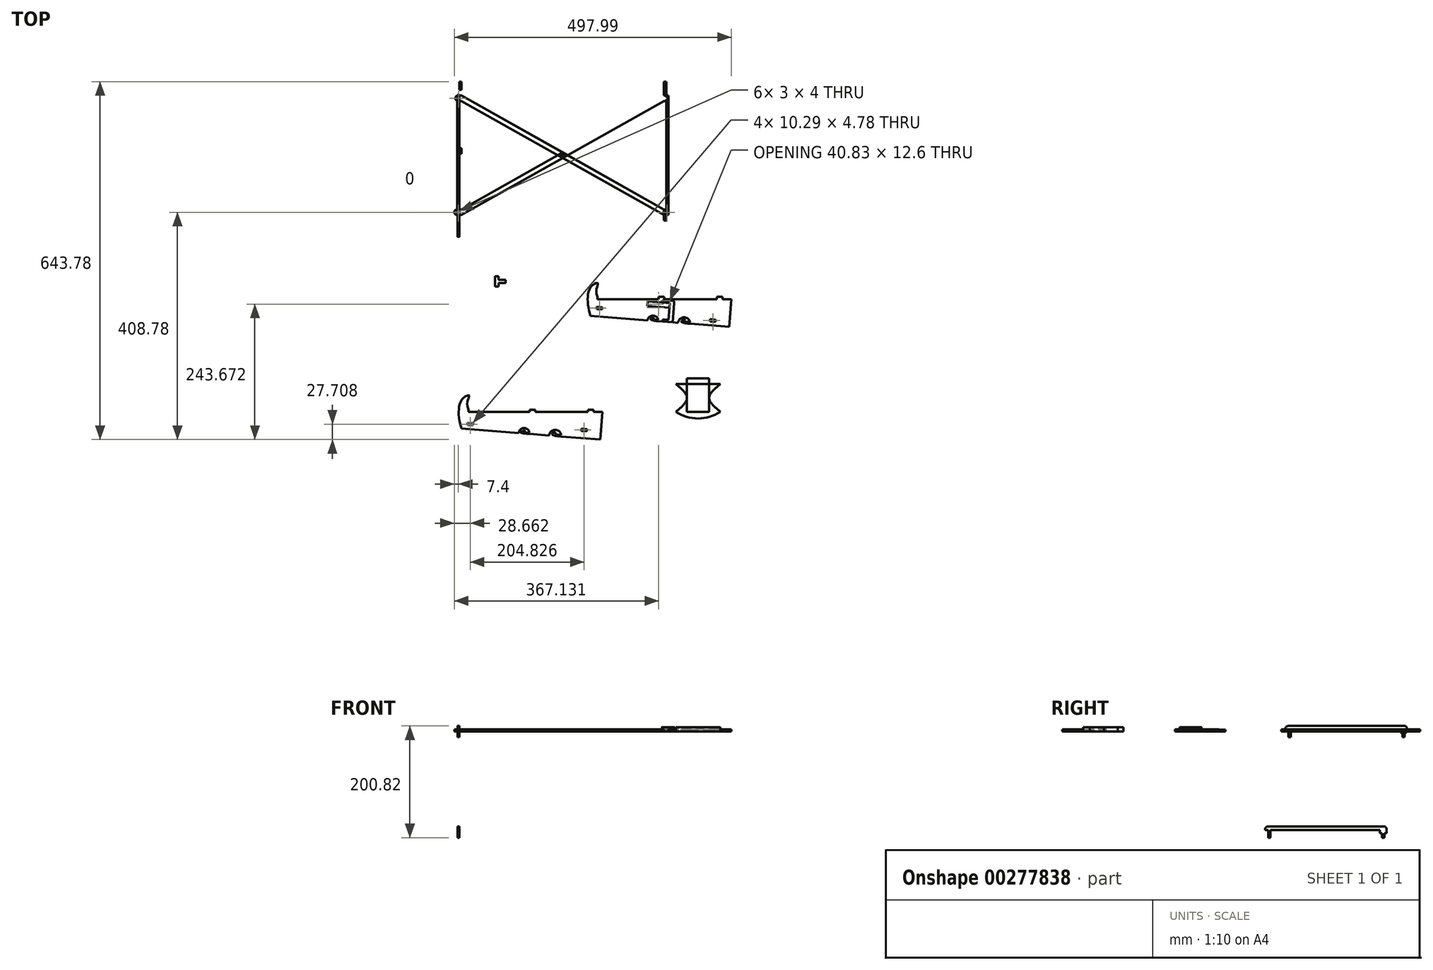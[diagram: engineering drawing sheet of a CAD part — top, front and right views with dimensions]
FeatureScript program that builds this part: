
annotation { "Feature Type Name" : "Feature", "Feature Type Description" : "" }
export const myFeature = defineFeature(function(context is Context, id is Id, definition is map)
    precondition{}
    {
        {
            var Q0;
            Q0=qCreatedBy(makeId("Top.planeOp"),FACE);
            var sketch = newSketch(context, id + "F0", { "sketchPlane" : qUnion([Q0])});
            skLineSegment(sketch, "E0.bottom", {"start": v(190, 125) * mm, "end": v(-190, 125) * mm});
            skLineSegment(sketch, "E0.top", {"start": v(190, -125) * mm, "end": v(-190, -125) * mm});
            skLineSegment(sketch, "E0.left", {"start": v(190, 125) * mm, "end": v(190, -125) * mm});
            skLineSegment(sketch, "E0.right", {"start": v(-190, 125) * mm, "end": v(-190, -125) * mm});
            skPoint(sketch, "E0.middle", {"position": v(0, 0) * mm});
            skLineSegment(sketch, "E1.right", {"start": v(-190, 125) * mm, "end": v(-190, -108) * mm});
            skLineSegment(sketch, "E2.bottom", {"start": v(-190, -125) * mm, "end": v(-186, -125) * mm});
            skLineSegment(sketch, "E2.top", {"start": v(-190, 125) * mm, "end": v(-186, 125) * mm});
            skLineSegment(sketch, "E2.left", {"start": v(-190, -125) * mm, "end": v(-190, -112) * mm});
            skLineSegment(sketch, "E2.right", {"start": v(-186, -125) * mm, "end": v(-186, -115) * mm});
            skLineSegment(sketch, "E3.bottom", {"start": v(190, -125) * mm, "end": v(186, -125) * mm});
            skLineSegment(sketch, "E3.top", {"start": v(190, 125) * mm, "end": v(186, 125) * mm});
            skLineSegment(sketch, "E3.left", {"start": v(190, -125) * mm, "end": v(190, 125) * mm});
            skLineSegment(sketch, "E3.right", {"start": v(186, -125) * mm, "end": v(186, 125) * mm});
            skLineSegment(sketch, "E4", {"start": v(49.8, -296.15) * mm, "end": v(152.32, -304.35) * mm});
            skLineSegment(sketch, "E5", {"start": v(299, -316.08) * mm, "end": v(303, -266.24) * mm});
            skLineSegment(sketch, "E6", {"start": v(303, -266.24) * mm, "end": v(287.2, -266.24) * mm});
            skLineSegment(sketch, "E7", {"start": v(52.2, -266.24) * mm, "end": v(49.8, -296.15) * mm, "construction": true});
            skLineSegment(sketch, "E8", {"start": v(0, 0) * mm, "end": v(0, 125) * mm, "construction": true});
            skLineSegment(sketch, "E9", {"start": v(0, 0) * mm, "end": v(0, -125) * mm, "construction": true});
            skLineSegment(sketch, "E10.bottom", {"start": v(-186, 125) * mm, "end": v(-182, 125) * mm});
            skLineSegment(sketch, "E10.top", {"start": v(-186, -125) * mm, "end": v(-182, -125) * mm});
            skLineSegment(sketch, "E10.left", {"start": v(-186, 125) * mm, "end": v(-186, 100) * mm});
            skLineSegment(sketch, "E10.right", {"start": v(-182, 125) * mm, "end": v(-182, 100) * mm});
            skLineSegment(sketch, "E11.MirrorCS", {"start": v(182, 125) * mm, "end": v(182, -125) * mm});
            skLineSegment(sketch, "E12", {"start": v(-186, -115) * mm, "end": v(-182, -115) * mm});
            skLineSegment(sketch, "E13", {"start": v(-186, 0) * mm, "end": v(186, 0) * mm, "construction": true});
            skLineSegment(sketch, "E14", {"start": v(-183.8, 0) * mm, "end": v(-183.8, 5) * mm, "construction": true});
            skLineSegment(sketch, "E15", {"start": v(-186, 5) * mm, "end": v(-182, 5) * mm});
            skLineSegment(sketch, "E16.MirrorCS", {"start": v(-186, -5) * mm, "end": v(-182, -5) * mm});
            skLineSegment(sketch, "E17", {"start": v(-186, 110) * mm, "end": v(-182, 110) * mm});
            skLineSegment(sketch, "E18", {"start": v(-186, 100) * mm, "end": v(-182, 100) * mm});
            skLineSegment(sketch, "E19", {"start": v(52.2, -266.24) * mm, "end": v(52.2, -242.24) * mm, "construction": true});
            skLineSegment(sketch, "E20", {"start": v(52.2, -242.24) * mm, "end": v(62.16, -243.04) * mm, "construction": true});
            skLineSegment(sketch, "E21", {"start": v(62.16, -243.04) * mm, "end": v(62.16, -266.24) * mm, "construction": true});
            skLineSegment(sketch, "E22.bottom", {"start": v(62.16, -266.24) * mm, "end": v(172.2, -266.24) * mm, "construction": true});
            skLineSegment(sketch, "E22.top", {"start": v(52.2, -262.24) * mm, "end": v(303, -262.24) * mm, "construction": true});
            skLineSegment(sketch, "E22.left", {"start": v(52.2, -266.24) * mm, "end": v(52.2, -262.24) * mm, "construction": true});
            skLineSegment(sketch, "E22.right", {"start": v(303, -266.24) * mm, "end": v(303, -262.24) * mm, "construction": true});
            skFitSpline(sketch, "E23", {"points": [v(49.8, -296.15) * mm, v(44.72, -265.8) * mm, v(52.2, -242.24) * mm, v(62.86, -237.24) * mm, v(62.38, -242.24) * mm, v(62.16, -262.24) * mm], "startDerivative": vector(-32.9, 108.57) * mm, "endDerivative": vector(52.9, -154.73) * mm});
            skLineSegment(sketch, "E24", {"start": v(62.16, -262.24) * mm, "end": v(62.16, -266.24) * mm});
            skLineSegment(sketch, "E25", {"start": v(302.2, -266.24) * mm, "end": v(302.2, -262.24) * mm, "construction": true});
            skLineSegment(sketch, "E26", {"start": v(287.2, -266.24) * mm, "end": v(287.2, -262.24) * mm});
            skLineSegment(sketch, "E27", {"start": v(287.2, -262.24) * mm, "end": v(277.2, -262.24) * mm});
            skLineSegment(sketch, "E28", {"start": v(277.2, -262.24) * mm, "end": v(277.2, -266.24) * mm});
            skLineSegment(sketch, "E29", {"start": v(182.2, -266.24) * mm, "end": v(182.2, -262.24) * mm});
            skLineSegment(sketch, "E30", {"start": v(172.2, -266.24) * mm, "end": v(172.2, -262.24) * mm});
            skLineSegment(sketch, "E31", {"start": v(172.2, -262.24) * mm, "end": v(182.2, -262.24) * mm});
            skLineSegment(sketch, "E32", {"start": v(-182, -105) * mm, "end": v(-186, -105) * mm});
            skLineSegment(sketch, "E33", {"start": v(-186, 90) * mm, "end": v(-182, 90) * mm});
            skLineSegment(sketch, "E34.MirrorCS", {"start": v(186, 125) * mm, "end": v(182, 125) * mm});
            skLineSegment(sketch, "E35.MirrorCS", {"start": v(186, -125) * mm, "end": v(182, -125) * mm});
            skLineSegment(sketch, "E36.MirrorCS", {"start": v(-190, -125) * mm, "end": v(190, -125) * mm});
            skLineSegment(sketch, "E37.MirrorCS", {"start": v(186, 110) * mm, "end": v(182, 110) * mm});
            skLineSegment(sketch, "E38.MirrorCS", {"start": v(183.8, 0) * mm, "end": v(183.8, 5) * mm, "construction": true});
            skLineSegment(sketch, "E39.MirrorCS", {"start": v(186, 100) * mm, "end": v(182, 100) * mm});
            skLineSegment(sketch, "E40.MirrorCS", {"start": v(182, -105) * mm, "end": v(186, -105) * mm});
            skLineSegment(sketch, "E41.MirrorCS", {"start": v(186, -5) * mm, "end": v(182, -5) * mm});
            skLineSegment(sketch, "E42.MirrorCS", {"start": v(186, 90) * mm, "end": v(182, 90) * mm});
            skLineSegment(sketch, "E43.MirrorCS", {"start": v(186, 5) * mm, "end": v(182, 5) * mm});
            skLineSegment(sketch, "E44.MirrorCS", {"start": v(186, -115) * mm, "end": v(182, -115) * mm});
            skLineSegment(sketch, "E45", {"start": v(-182, -115) * mm, "end": v(182, 90) * mm});
            skLineSegment(sketch, "E46", {"start": v(-182, -105) * mm, "end": v(182, 100) * mm});
            skLineSegment(sketch, "E47", {"start": v(-182, 90) * mm, "end": v(182, -115) * mm});
            skLineSegment(sketch, "E48", {"start": v(182, -105) * mm, "end": v(-182, 100) * mm});
            skLineSegment(sketch, "E49.trimOffspring", {"start": v(-186, -115) * mm, "end": v(-186, -125) * mm});
            skLineSegment(sketch, "E50.trimOffspring", {"start": v(-186, -105) * mm, "end": v(-186, 90) * mm});
            skLineSegment(sketch, "E51", {"start": v(-186, -105) * mm, "end": v(-190, -105) * mm});
            skLineSegment(sketch, "E52", {"start": v(-186, -115) * mm, "end": v(-190, -115) * mm});
            skArc(sketch, "E53", {"start": v(-190, -105) * mm, "mid": v(-195, -110) * mm, "end": v(-190, -115) * mm});
            skArc(sketch, "E54", {"start": v(-190, 99.76) * mm, "mid": v(-193.01, 94.84) * mm, "end": v(-190, 89.93) * mm});
            skLineSegment(sketch, "E55.trimOffspring", {"start": v(-186, 100) * mm, "end": v(-186, 125) * mm});
            skLineSegment(sketch, "E56.trimOffspring", {"start": v(-186, 90) * mm, "end": v(-186, -105) * mm});
            skLineSegment(sketch, "E57.trimOffspring", {"start": v(-182, 90) * mm, "end": v(-182, -125) * mm});
            skLineSegment(sketch, "E58.MirrorCS", {"start": v(186, -125) * mm, "end": v(186, -115) * mm});
            skLineSegment(sketch, "E59.MirrorCS", {"start": v(186, -115) * mm, "end": v(186, -125) * mm});
            skLineSegment(sketch, "E60.MirrorCS", {"start": v(186, -115) * mm, "end": v(190, -115) * mm});
            skLineSegment(sketch, "E61.MirrorCS", {"start": v(186, -105) * mm, "end": v(190, -105) * mm});
            skArc(sketch, "E62.MirrorCS", {"start": v(190, -105) * mm, "mid": v(195, -110) * mm, "end": v(190, -115) * mm});
            skLineSegment(sketch, "E63.MirrorCS", {"start": v(186, 100) * mm, "end": v(186, 125) * mm});
            skLineSegment(sketch, "E64.MirrorCS", {"start": v(182, 125) * mm, "end": v(182, 100) * mm});
            skLineSegment(sketch, "E65.MirrorCS", {"start": v(186, 125) * mm, "end": v(186, 100) * mm});
            skArc(sketch, "E66.MirrorCS", {"start": v(190, 99.76) * mm, "mid": v(193.01, 94.84) * mm, "end": v(190, 89.93) * mm});
            skLineSegment(sketch, "E67.MirrorCS", {"start": v(186, 90) * mm, "end": v(186, -105) * mm});
            skLineSegment(sketch, "E68.MirrorCS", {"start": v(186, -105) * mm, "end": v(186, 90) * mm});
            skLineSegment(sketch, "E69.MirrorCS", {"start": v(182, 90) * mm, "end": v(182, -125) * mm});
            skLineSegment(sketch, "E70", {"start": v(186, 100) * mm, "end": v(190, 99.76) * mm});
            skLineSegment(sketch, "E71", {"start": v(186, 90) * mm, "end": v(190, 89.93) * mm});
            skLineSegment(sketch, "E72", {"start": v(-186, 90) * mm, "end": v(-190, 89.93) * mm});
            skLineSegment(sketch, "E73", {"start": v(-186, 100) * mm, "end": v(-190, 99.76) * mm});
            skLineSegment(sketch, "E74.trimOffspring", {"start": v(182.2, -266.24) * mm, "end": v(277.2, -266.24) * mm, "construction": true});
            skLineSegment(sketch, "E75.trimOffspring", {"start": v(172.2, -266.24) * mm, "end": v(62.16, -266.24) * mm});
            skLineSegment(sketch, "E76.trimOffspring", {"start": v(287.2, -266.24) * mm, "end": v(303, -266.24) * mm, "construction": true});
            skLineSegment(sketch, "E77.trimOffspring", {"start": v(277.2, -266.24) * mm, "end": v(182.2, -266.24) * mm});
            skLineSegment(sketch, "E78", {"start": v(50.88, -283.2) * mm, "end": v(300.08, -303.13) * mm, "construction": true});
            skLineSegment(sketch, "E79", {"start": v(51.2, -279.2) * mm, "end": v(197.94, -290.94) * mm, "construction": true});
            skLineSegment(sketch, "E80", {"start": v(275.12, -301.13) * mm, "end": v(275.44, -297.14) * mm});
            skLineSegment(sketch, "E81", {"start": v(275.44, -297.14) * mm, "end": v(265.47, -296.35) * mm});
            skLineSegment(sketch, "E82", {"start": v(265.47, -296.35) * mm, "end": v(265.15, -300.33) * mm});
            skLineSegment(sketch, "E83", {"start": v(265.15, -300.33) * mm, "end": v(275.12, -301.13) * mm});
            skLineSegment(sketch, "E84", {"start": v(60.8, -283.99) * mm, "end": v(61.13, -280) * mm});
            skLineSegment(sketch, "E85", {"start": v(71.1, -280.8) * mm, "end": v(70.77, -284.78) * mm});
            skLineSegment(sketch, "E86", {"start": v(61.13, -280) * mm, "end": v(71.1, -280.8) * mm});
            skLineSegment(sketch, "E87", {"start": v(70.77, -284.78) * mm, "end": v(60.8, -283.99) * mm});
            skLineSegment(sketch, "E88", {"start": v(265.47, -296.35) * mm, "end": v(264.12, -313.3) * mm, "construction": true});
            skLineSegment(sketch, "E89", {"start": v(275.44, -297.14) * mm, "end": v(274.09, -314.1) * mm, "construction": true});
            skLineSegment(sketch, "E90", {"start": v(264.68, -306.32) * mm, "end": v(274.64, -307.11) * mm});
            skLineSegment(sketch, "E91", {"start": v(265, -302.33) * mm, "end": v(274.96, -303.13) * mm});
            skLineSegment(sketch, "E92", {"start": v(265, -302.33) * mm, "end": v(264.68, -306.32) * mm});
            skLineSegment(sketch, "E93", {"start": v(274.96, -303.13) * mm, "end": v(274.64, -307.11) * mm});
            skLineSegment(sketch, "E94", {"start": v(61.13, -280) * mm, "end": v(59.77, -296.95) * mm, "construction": true});
            skLineSegment(sketch, "E95", {"start": v(60.65, -285.98) * mm, "end": v(70.62, -286.78) * mm});
            skLineSegment(sketch, "E96", {"start": v(60.33, -289.97) * mm, "end": v(70.3, -290.77) * mm});
            skLineSegment(sketch, "E97", {"start": v(70.3, -290.77) * mm, "end": v(70.62, -286.78) * mm});
            skLineSegment(sketch, "E98", {"start": v(60.65, -285.98) * mm, "end": v(60.33, -289.97) * mm});
            skLineSegment(sketch, "E99", {"start": v(-182, -498.85) * mm, "end": v(-79.55, -507.04) * mm});
            skLineSegment(sketch, "E100", {"start": v(67.2, -518.78) * mm, "end": v(71.18, -468.94) * mm});
            skLineSegment(sketch, "E101", {"start": v(71.18, -468.94) * mm, "end": v(55.38, -468.94) * mm});
            skLineSegment(sketch, "E102", {"start": v(-179.62, -468.94) * mm, "end": v(-182, -498.85) * mm, "construction": true});
            skLineSegment(sketch, "E103", {"start": v(-179.62, -468.94) * mm, "end": v(-179.62, -444.94) * mm, "construction": true});
            skLineSegment(sketch, "E104", {"start": v(-179.62, -444.94) * mm, "end": v(-169.65, -445.74) * mm, "construction": true});
            skLineSegment(sketch, "E105", {"start": v(-169.65, -445.74) * mm, "end": v(-169.65, -468.94) * mm, "construction": true});
            skLineSegment(sketch, "E106.bottom", {"start": v(-169.65, -468.94) * mm, "end": v(-59.62, -468.94) * mm, "construction": true});
            skLineSegment(sketch, "E106.top", {"start": v(-179.62, -464.94) * mm, "end": v(71.18, -464.94) * mm, "construction": true});
            skLineSegment(sketch, "E106.left", {"start": v(-179.62, -468.94) * mm, "end": v(-179.62, -464.94) * mm, "construction": true});
            skLineSegment(sketch, "E106.right", {"start": v(71.18, -468.94) * mm, "end": v(71.18, -464.94) * mm, "construction": true});
            skFitSpline(sketch, "E107", {"points": [v(-182, -498.85) * mm, v(-187.09, -467.99) * mm, v(-179.62, -444.94) * mm, v(-168.95, -439.42) * mm, v(-169.43, -444.94) * mm, v(-169.65, -464.94) * mm], "startDerivative": vector(-32.9, 108.57) * mm, "endDerivative": vector(52.9, -154.73) * mm});
            skLineSegment(sketch, "E108", {"start": v(-169.65, -464.94) * mm, "end": v(-169.65, -468.94) * mm});
            skLineSegment(sketch, "E109", {"start": v(70.38, -468.94) * mm, "end": v(70.38, -464.94) * mm, "construction": true});
            skLineSegment(sketch, "E110", {"start": v(55.38, -468.94) * mm, "end": v(55.38, -464.94) * mm});
            skLineSegment(sketch, "E111", {"start": v(55.38, -464.94) * mm, "end": v(45.38, -464.94) * mm});
            skLineSegment(sketch, "E112", {"start": v(45.38, -464.94) * mm, "end": v(45.38, -468.94) * mm});
            skLineSegment(sketch, "E113", {"start": v(-49.62, -468.94) * mm, "end": v(-49.62, -464.94) * mm});
            skLineSegment(sketch, "E114", {"start": v(-59.62, -468.94) * mm, "end": v(-59.62, -464.94) * mm});
            skLineSegment(sketch, "E115", {"start": v(-59.62, -464.94) * mm, "end": v(-49.62, -464.94) * mm});
            skLineSegment(sketch, "E116.trimOffspring", {"start": v(-49.62, -468.94) * mm, "end": v(45.38, -468.94) * mm, "construction": true});
            skLineSegment(sketch, "E117.trimOffspring", {"start": v(-59.62, -468.94) * mm, "end": v(-169.65, -468.94) * mm});
            skLineSegment(sketch, "E118.trimOffspring", {"start": v(55.38, -468.94) * mm, "end": v(71.18, -468.94) * mm, "construction": true});
            skLineSegment(sketch, "E119.trimOffspring", {"start": v(45.38, -468.94) * mm, "end": v(-49.62, -468.94) * mm});
            skLineSegment(sketch, "E120", {"start": v(-180.97, -485.89) * mm, "end": v(68.23, -505.82) * mm, "construction": true});
            skLineSegment(sketch, "E121", {"start": v(-180.65, -481.9) * mm, "end": v(68.55, -501.84) * mm, "construction": true});
            skLineSegment(sketch, "E122", {"start": v(43.31, -503.83) * mm, "end": v(43.63, -499.84) * mm});
            skLineSegment(sketch, "E123", {"start": v(43.63, -499.84) * mm, "end": v(33.66, -499.05) * mm});
            skLineSegment(sketch, "E124", {"start": v(33.66, -499.05) * mm, "end": v(33.34, -503.03) * mm});
            skLineSegment(sketch, "E125", {"start": v(33.34, -503.03) * mm, "end": v(43.31, -503.83) * mm});
            skLineSegment(sketch, "E126", {"start": v(-171, -486.69) * mm, "end": v(-170.68, -482.7) * mm});
            skLineSegment(sketch, "E127", {"start": v(-160.72, -483.5) * mm, "end": v(-161.03, -487.48) * mm});
            skLineSegment(sketch, "E128", {"start": v(-170.68, -482.7) * mm, "end": v(-160.72, -483.5) * mm});
            skLineSegment(sketch, "E129", {"start": v(-161.03, -487.48) * mm, "end": v(-171, -486.69) * mm});
            skLineSegment(sketch, "E130", {"start": v(33.66, -499.05) * mm, "end": v(32.3, -516) * mm, "construction": true});
            skLineSegment(sketch, "E131", {"start": v(43.63, -499.84) * mm, "end": v(42.28, -516.79) * mm, "construction": true});
            skLineSegment(sketch, "E132", {"start": v(32.87, -509.01) * mm, "end": v(42.83, -509.81) * mm});
            skLineSegment(sketch, "E133", {"start": v(33.19, -505.03) * mm, "end": v(43.15, -505.82) * mm});
            skLineSegment(sketch, "E134", {"start": v(33.19, -505.03) * mm, "end": v(32.87, -509.01) * mm});
            skLineSegment(sketch, "E135", {"start": v(43.15, -505.82) * mm, "end": v(42.83, -509.81) * mm});
            skLineSegment(sketch, "E136", {"start": v(-170.68, -482.7) * mm, "end": v(-172.04, -499.64) * mm, "construction": true});
            skLineSegment(sketch, "E137", {"start": v(-171.16, -488.68) * mm, "end": v(-161.2, -489.48) * mm});
            skLineSegment(sketch, "E138", {"start": v(-171.48, -492.67) * mm, "end": v(-161.51, -493.46) * mm});
            skLineSegment(sketch, "E139", {"start": v(-161.51, -493.46) * mm, "end": v(-161.2, -489.48) * mm});
            skLineSegment(sketch, "E140", {"start": v(-171.16, -488.68) * mm, "end": v(-171.48, -492.67) * mm});
            skLineSegment(sketch, "E141.MirrorCS", {"start": v(-190, -125) * mm, "end": v(-190, 125) * mm});
            skLineSegment(sketch, "E142.trimOffspring", {"start": v(-190, -108) * mm, "end": v(-190, 125) * mm});
            skLineSegment(sketch, "E143.trimOffspring", {"start": v(-190, -110) * mm, "end": v(-190, -125) * mm});
            skLineSegment(sketch, "E144.bottom", {"start": v(-189, 96.84) * mm, "end": v(-186, 96.84) * mm, "construction": true});
            skLineSegment(sketch, "E144.top", {"start": v(-189, 92.84) * mm, "end": v(-186, 92.84) * mm, "construction": true});
            skLineSegment(sketch, "E144.left", {"start": v(-189, 96.84) * mm, "end": v(-189, 92.84) * mm, "construction": true});
            skLineSegment(sketch, "E144.right", {"start": v(-186, 96.84) * mm, "end": v(-186, 92.84) * mm, "construction": true});
            skLineSegment(sketch, "E145.MirrorCS", {"start": v(189, 92.84) * mm, "end": v(186, 92.84) * mm});
            skLineSegment(sketch, "E146.MirrorCS", {"start": v(189, 96.84) * mm, "end": v(186, 96.84) * mm});
            skLineSegment(sketch, "E147.MirrorCS", {"start": v(189, 96.84) * mm, "end": v(189, 92.84) * mm});
            skLineSegment(sketch, "E148.MirrorCS", {"start": v(186, 96.84) * mm, "end": v(186, 92.84) * mm});
            skLineSegment(sketch, "E149.bottom", {"start": v(-186.1, -112) * mm, "end": v(-189.1, -112) * mm});
            skLineSegment(sketch, "E149.top", {"start": v(-186.1, -108) * mm, "end": v(-189.1, -108) * mm});
            skLineSegment(sketch, "E149.left", {"start": v(-186.1, -112) * mm, "end": v(-186.1, -108) * mm});
            skLineSegment(sketch, "E149.right", {"start": v(-189.1, -112) * mm, "end": v(-189.1, -108) * mm});
            skLineSegment(sketch, "E150", {"start": v(-186, -105) * mm, "end": v(-186, -115) * mm, "construction": true});
            skLineSegment(sketch, "E151.MirrorCS", {"start": v(190, -108) * mm, "end": v(190, 125) * mm});
            skLineSegment(sketch, "E152.MirrorCS", {"start": v(190, -110) * mm, "end": v(190, -125) * mm});
            skLineSegment(sketch, "E153.MirrorCS", {"start": v(186, -105) * mm, "end": v(186, -115) * mm, "construction": true});
            skLineSegment(sketch, "E154.MirrorCS", {"start": v(190, 125) * mm, "end": v(190, -108) * mm});
            skLineSegment(sketch, "E155.MirrorCS", {"start": v(186.1, -112) * mm, "end": v(189.1, -112) * mm});
            skLineSegment(sketch, "E156.MirrorCS", {"start": v(190, -125) * mm, "end": v(190, -112) * mm});
            skLineSegment(sketch, "E157.MirrorCS", {"start": v(186.1, -112) * mm, "end": v(186.1, -108) * mm});
            skLineSegment(sketch, "E158.MirrorCS", {"start": v(189.1, -112) * mm, "end": v(189.1, -108) * mm});
            skLineSegment(sketch, "E159.MirrorCS", {"start": v(186.1, -108) * mm, "end": v(189.1, -108) * mm});
            skLineSegment(sketch, "E160", {"start": v(-186, 90) * mm, "end": v(-186, 100) * mm, "construction": true});
            skLineSegment(sketch, "E161.bottom", {"start": v(-189, 96.84) * mm, "end": v(-186, 96.84) * mm});
            skLineSegment(sketch, "E161.top", {"start": v(-189, 92.84) * mm, "end": v(-186, 92.84) * mm});
            skLineSegment(sketch, "E161.left", {"start": v(-189, 96.84) * mm, "end": v(-189, 92.84) * mm});
            skLineSegment(sketch, "E161.right", {"start": v(-186, 96.84) * mm, "end": v(-186, 92.84) * mm});
            skLineSegment(sketch, "E162", {"start": v(8.88, -7.5) * mm, "end": v(-8.88, -7.5) * mm, "construction": true});
            skLineSegment(sketch, "E163.bottom", {"start": v(3, -9) * mm, "end": v(-3, -9) * mm});
            skLineSegment(sketch, "E163.top", {"start": v(3, -6) * mm, "end": v(-3, -6) * mm});
            skLineSegment(sketch, "E163.left", {"start": v(3, -9) * mm, "end": v(3, -6) * mm});
            skLineSegment(sketch, "E163.right", {"start": v(-3, -9) * mm, "end": v(-3, -6) * mm});
            skPoint(sketch, "E163.middle", {"position": v(0, -7.5) * mm});
            skLineSegment(sketch, "E164.bottom", {"start": v(-115.58, -237.46) * mm, "end": v(-102.58, -237.46) * mm});
            skLineSegment(sketch, "E164.top", {"start": v(-115.58, -231.46) * mm, "end": v(-102.58, -231.46) * mm});
            skLineSegment(sketch, "E164.left", {"start": v(-121.58, -237.46) * mm, "end": v(-121.58, -231.46) * mm});
            skLineSegment(sketch, "E164.right", {"start": v(-102.58, -237.46) * mm, "end": v(-102.58, -231.46) * mm});
            skPoint(sketch, "E164.middle", {"position": v(-112.08, -234.46) * mm});
            skLineSegment(sketch, "E165.top", {"start": v(-121.58, -243.46) * mm, "end": v(-115.58, -243.46) * mm});
            skLineSegment(sketch, "E165.left", {"start": v(-121.58, -231.46) * mm, "end": v(-121.58, -243.46) * mm});
            skLineSegment(sketch, "E165.right", {"start": v(-115.58, -231.46) * mm, "end": v(-115.58, -243.46) * mm});
            skLineSegment(sketch, "E166", {"start": v(-105.58, -231.46) * mm, "end": v(-105.58, -237.46) * mm, "construction": true});
            skLineSegment(sketch, "E167", {"start": v(-121.58, -231.46) * mm, "end": v(-121.58, -225.46) * mm});
            skLineSegment(sketch, "E168", {"start": v(-121.58, -225.46) * mm, "end": v(-115.58, -225.46) * mm});
            skLineSegment(sketch, "E169", {"start": v(-115.58, -225.46) * mm, "end": v(-115.58, -231.46) * mm});
            skLineSegment(sketch, "E170", {"start": v(191.59, -281.4) * mm, "end": v(151.72, -278.22) * mm});
            skLineSegment(sketch, "E171", {"start": v(151.72, -278.22) * mm, "end": v(152.35, -270.24) * mm});
            skLineSegment(sketch, "E172", {"start": v(152.35, -270.24) * mm, "end": v(192.23, -273.43) * mm});
            skLineSegment(sketch, "E173", {"start": v(192.23, -273.43) * mm, "end": v(191.59, -281.4) * mm});
            skLineSegment(sketch, "E174.trimOffspring", {"start": v(237.81, -294.13) * mm, "end": v(300.4, -299.14) * mm, "construction": true});
            skLineSegment(sketch, "E175", {"start": v(200.25, -273.43) * mm, "end": v(197.49, -307.96) * mm});
            skLineSegment(sketch, "E176", {"start": v(179.56, -306.53) * mm, "end": v(179.88, -302.54) * mm});
            skLineSegment(sketch, "E177", {"start": v(179.88, -302.54) * mm, "end": v(189.85, -303.34) * mm});
            skLineSegment(sketch, "E178", {"start": v(179.56, -306.53) * mm, "end": v(197.49, -307.96) * mm});
            skLineSegment(sketch, "E179", {"start": v(191.59, -281.4) * mm, "end": v(189.52, -307.32) * mm});
            skLineSegment(sketch, "E180", {"start": v(181.86, -302.7) * mm, "end": v(181.54, -306.69) * mm});
            skLineSegment(sketch, "E181.bottom", {"start": v(223.2, -408.84) * mm, "end": v(263.2, -408.84) * mm});
            skLineSegment(sketch, "E181.top", {"start": v(223.2, -418.84) * mm, "end": v(263.2, -418.84) * mm});
            skLineSegment(sketch, "E181.left", {"start": v(223.2, -408.84) * mm, "end": v(223.2, -418.84) * mm});
            skLineSegment(sketch, "E181.right", {"start": v(263.2, -408.84) * mm, "end": v(263.2, -418.84) * mm});
            skLineSegment(sketch, "E182.bottom", {"start": v(223.2, -418.84) * mm, "end": v(271.68, -418.84) * mm});
            skLineSegment(sketch, "E182.top", {"start": v(223.2, -468.84) * mm, "end": v(263.2, -468.84) * mm});
            skLineSegment(sketch, "E182.left", {"start": v(223.2, -418.84) * mm, "end": v(223.2, -468.84) * mm});
            skLineSegment(sketch, "E183", {"start": v(263.2, -418.84) * mm, "end": v(283.2, -418.84) * mm});
            skLineSegment(sketch, "E184", {"start": v(223.2, -418.84) * mm, "end": v(203.2, -418.84) * mm});
            skLineSegment(sketch, "E185", {"start": v(263.2, -418.84) * mm, "end": v(263.2, -468.84) * mm});
            skLineSegment(sketch, "E186", {"start": v(203.2, -468.84) * mm, "end": v(223.2, -468.84) * mm});
            skFitSpline(sketch, "E187", {"points": [v(203.2, -418.84) * mm, v(223.2, -443.84) * mm, v(203.2, -468.84) * mm], "startDerivative": vector(60, -50) * mm, "endDerivative": vector(-60, -50) * mm});
            skLineSegment(sketch, "E188", {"start": v(243.2, -408.84) * mm, "end": v(243.2, -468.84) * mm, "construction": true});
            skFitSpline(sketch, "E189.MirrorCS", {"points": [v(283.2, -418.84) * mm, v(263.2, -443.84) * mm, v(283.2, -468.84) * mm], "startDerivative": vector(-60, -50) * mm, "endDerivative": vector(60, -50) * mm});
            skLineSegment(sketch, "E190.MirrorCS", {"start": v(283.2, -468.84) * mm, "end": v(263.2, -468.84) * mm});
            skArc(sketch, "E191", {"start": v(203.2, -468.84) * mm, "mid": v(243.2, -480.84) * mm, "end": v(283.2, -468.84) * mm});
            skLineSegment(sketch, "E192", {"start": v(186.56, -268.97) * mm, "end": v(182.58, -268.65) * mm});
            skLineSegment(sketch, "E193", {"start": v(182.58, -268.65) * mm, "end": v(182.26, -272.64) * mm});
            skLineSegment(sketch, "E194", {"start": v(192.23, -273.43) * mm, "end": v(192.55, -269.45) * mm});
            skLineSegment(sketch, "E195", {"start": v(192.55, -269.45) * mm, "end": v(186.56, -268.97) * mm});
            skLineSegment(sketch, "E196", {"start": v(184.57, -268.8) * mm, "end": v(184.25, -272.8) * mm});
            skFitSpline(sketch, "E197", {"points": [v(192.55, -269.45) * mm, v(199.31, -269.66) * mm, v(200.25, -273.43) * mm], "startDerivative": vector(15.87, 5.36) * mm, "endDerivative": vector(-1.15, -11.12) * mm});
            skLineSegment(sketch, "E198", {"start": v(182.58, -268.65) * mm, "end": v(180.58, -268.49) * mm});
            skFitSpline(sketch, "E199", {"points": [v(180.58, -268.49) * mm, v(178.6, -272.34) * mm], "startDerivative": vector(-6.52, -3.18) * mm, "endDerivative": vector(0.58, -3.67) * mm});
            skLineSegment(sketch, "E200", {"start": v(172.2, -266.24) * mm, "end": v(172.2, -305.94) * mm, "construction": true});
            skArc(sketch, "E201", {"start": v(171.92, -303.6) * mm, "mid": v(161.81, -295.95) * mm, "end": v(152.32, -304.35) * mm});
            skLineSegment(sketch, "E202", {"start": v(-59.62, -468.94) * mm, "end": v(-59.62, -507.28) * mm, "construction": true});
            skArc(sketch, "E203", {"start": v(-2.9, -510.02) * mm, "mid": v(-14.37, -501.34) * mm, "end": v(-24.62, -511.44) * mm});
            skLineSegment(sketch, "E204.trimOffspring", {"start": v(-59.62, -508.64) * mm, "end": v(-24.62, -511.44) * mm});
            skLineSegment(sketch, "E205.trimOffspring", {"start": v(-2.69, -513.2) * mm, "end": v(67.2, -518.78) * mm});
            skFitSpline(sketch, "E206", {"points": [v(-2.69, -513.2) * mm, v(-15.78, -511.43) * mm, v(-19.23, -509.19) * mm, v(-17.76, -506.59) * mm, v(-13.38, -506.25) * mm, v(-14.8, -508.21) * mm, v(-2.69, -511.44) * mm], "startDerivative": vector(-44.09, 4) * mm, "endDerivative": vector(41.48, -21.36) * mm});
            skFitSpline(sketch, "E207", {"points": [v(-59.62, -508.64) * mm, v(-75.41, -506.11) * mm, v(-74.67, -504.74) * mm, v(-71.74, -503.03) * mm, v(-68.32, -502.54) * mm, v(-68.95, -504.77) * mm, v(-59.72, -506.6) * mm], "startDerivative": vector(-44.09, 4) * mm, "endDerivative": vector(48.5, -6.14) * mm});
            skArc(sketch, "E208.trimOffspring", {"start": v(-59.72, -506.6) * mm, "mid": v(-69.83, -498.12) * mm, "end": v(-79.55, -507.04) * mm});
            skFitSpline(sketch, "E209", {"points": [v(172.13, -305.97) * mm, v(161.88, -304.33) * mm, v(157.84, -302.36) * mm, v(159.8, -299.35) * mm, v(163.27, -298.58) * mm, v(162.56, -301.53) * mm, v(172.2, -303.64) * mm], "startDerivative": vector(-44.09, 4) * mm, "endDerivative": vector(48.5, -6.14) * mm});
            skLineSegment(sketch, "E210.trimOffspring", {"start": v(170.42, -305.8) * mm, "end": v(207.13, -308.73) * mm});
            skArc(sketch, "E211", {"start": v(228.8, -307.7) * mm, "mid": v(217.53, -299.03) * mm, "end": v(207.13, -308.73) * mm});
            skFitSpline(sketch, "E212", {"points": [v(229.05, -310.49) * mm, v(216.5, -308.58) * mm, v(212.99, -306.61) * mm, v(215.8, -303.95) * mm, v(219.36, -302.92) * mm, v(218.14, -305.54) * mm, v(229.73, -307.84) * mm], "startDerivative": vector(-44.09, 4) * mm, "endDerivative": vector(48.04, -9.09) * mm});
            skLineSegment(sketch, "E213.trimOffspring", {"start": v(229.05, -310.49) * mm, "end": v(299, -316.08) * mm});
            skLineSegment(sketch, "E214", {"start": v(-8.02, -510.02) * mm, "end": v(-2.9, -510.02) * mm});
            skLineSegment(sketch, "E215", {"start": v(-170.68, -482.7) * mm, "end": v(-169.97, -473.73) * mm, "construction": true});
            skLineSegment(sketch, "E216", {"start": v(-169.97, -473.73) * mm, "end": v(44.35, -490.87) * mm, "construction": true});
            skLineSegment(sketch, "E217", {"start": v(44.35, -490.87) * mm, "end": v(43.63, -499.84) * mm, "construction": true});
            skLineSegment(sketch, "E218", {"start": v(-169.97, -473.73) * mm, "end": v(-169.65, -468.94) * mm, "construction": true});
            skLineSegment(sketch, "E219", {"start": v(458.34, 154.63) * mm, "end": v(462.34, 154.63) * mm});
            skLineSegment(sketch, "E220", {"start": v(458.34, 144.63) * mm, "end": v(462.34, 144.63) * mm});
            skLineSegment(sketch, "E221", {"start": v(462.34, 144.63) * mm, "end": v(826.34, -60.37) * mm});
            skLineSegment(sketch, "E222", {"start": v(826.34, -50.37) * mm, "end": v(462.34, 154.63) * mm});
            skArc(sketch, "E223", {"start": v(454.34, 154.39) * mm, "mid": v(451.32, 149.47) * mm, "end": v(454.34, 144.56) * mm});
            skLineSegment(sketch, "E224.MirrorCS", {"start": v(830.34, -60.37) * mm, "end": v(834.34, -60.37) * mm});
            skLineSegment(sketch, "E225.MirrorCS", {"start": v(830.34, -60.37) * mm, "end": v(826.34, -60.37) * mm});
            skLineSegment(sketch, "E226.MirrorCS", {"start": v(826.34, -50.37) * mm, "end": v(830.34, -50.37) * mm});
            skLineSegment(sketch, "E227.MirrorCS", {"start": v(830.34, -50.37) * mm, "end": v(834.34, -50.37) * mm});
            skArc(sketch, "E228.MirrorCS", {"start": v(834.34, -50.37) * mm, "mid": v(839.34, -55.37) * mm, "end": v(834.34, -60.37) * mm});
            skLineSegment(sketch, "E229", {"start": v(458.34, 144.63) * mm, "end": v(454.34, 144.56) * mm});
            skLineSegment(sketch, "E230", {"start": v(458.34, 154.63) * mm, "end": v(454.34, 154.39) * mm});
            skLineSegment(sketch, "E231.bottom", {"start": v(455.34, 151.47) * mm, "end": v(458.34, 151.47) * mm, "construction": true});
            skLineSegment(sketch, "E231.top", {"start": v(455.34, 147.47) * mm, "end": v(458.34, 147.47) * mm, "construction": true});
            skLineSegment(sketch, "E231.left", {"start": v(455.34, 151.47) * mm, "end": v(455.34, 147.47) * mm, "construction": true});
            skLineSegment(sketch, "E232.MirrorCS", {"start": v(830.44, -57.37) * mm, "end": v(833.44, -57.37) * mm});
            skLineSegment(sketch, "E233.MirrorCS", {"start": v(830.44, -57.37) * mm, "end": v(830.44, -53.37) * mm});
            skLineSegment(sketch, "E234.MirrorCS", {"start": v(833.44, -57.37) * mm, "end": v(833.44, -53.37) * mm});
            skLineSegment(sketch, "E235.MirrorCS", {"start": v(830.44, -53.37) * mm, "end": v(833.44, -53.37) * mm});
            skLineSegment(sketch, "E236", {"start": v(458.34, 144.63) * mm, "end": v(458.34, 154.63) * mm, "construction": true});
            skLineSegment(sketch, "E237.bottom", {"start": v(647.34, 45.63) * mm, "end": v(641.34, 45.63) * mm});
            skLineSegment(sketch, "E237.top", {"start": v(647.34, 48.63) * mm, "end": v(641.34, 48.63) * mm});
            skLineSegment(sketch, "E237.left", {"start": v(647.34, 45.63) * mm, "end": v(647.34, 48.63) * mm});
            skLineSegment(sketch, "E237.right", {"start": v(641.34, 45.63) * mm, "end": v(641.34, 48.63) * mm});
            skLineSegment(sketch, "E238.bottom", {"start": v(455.34, 151.47) * mm, "end": v(458.34, 151.47) * mm});
            skLineSegment(sketch, "E238.top", {"start": v(455.34, 147.47) * mm, "end": v(458.34, 147.47) * mm});
            skLineSegment(sketch, "E238.left", {"start": v(455.34, 151.47) * mm, "end": v(455.34, 147.47) * mm});
            skLineSegment(sketch, "E238.right", {"start": v(458.34, 151.47) * mm, "end": v(458.34, 147.47) * mm});
            skLineSegment(sketch, "E239", {"start": v(462.1, 74.96) * mm, "end": v(464.4, 71.68) * mm});
            skLineSegment(sketch, "E240", {"start": v(472.58, 77.41) * mm, "end": v(470.29, 80.7) * mm});
            skLineSegment(sketch, "E241", {"start": v(464.4, 71.68) * mm, "end": v(841.1, -108.9) * mm});
            skLineSegment(sketch, "E242", {"start": v(472.58, 77.41) * mm, "end": v(849.3, -103.17) * mm});
            skLineSegment(sketch, "E243", {"start": v(470.29, 80.7) * mm, "end": v(468, 83.97) * mm});
            skLineSegment(sketch, "E244", {"start": v(462.1, 74.96) * mm, "end": v(459.8, 78.23) * mm});
            skArc(sketch, "E245", {"start": v(468, 83.97) * mm, "mid": v(461.03, 85.2) * mm, "end": v(459.8, 78.23) * mm});
            skLineSegment(sketch, "E246.MirrorCS", {"start": v(851.59, -106.45) * mm, "end": v(849.3, -103.17) * mm});
            skLineSegment(sketch, "E247.MirrorCS", {"start": v(843.4, -112.19) * mm, "end": v(841.1, -108.9) * mm});
            skArc(sketch, "E248.MirrorCS", {"start": v(853.68, -109.87) * mm, "mid": v(851.38, -115.15) * mm, "end": v(845.63, -115.5) * mm});
            skLineSegment(sketch, "E249", {"start": v(851.59, -106.45) * mm, "end": v(853.68, -109.87) * mm});
            skLineSegment(sketch, "E250", {"start": v(843.4, -112.19) * mm, "end": v(845.63, -115.5) * mm});
            skLineSegment(sketch, "E251.MirrorCS", {"start": v(847.44, -113.01) * mm, "end": v(845.72, -110.56) * mm});
            skLineSegment(sketch, "E252.MirrorCS", {"start": v(850.72, -110.72) * mm, "end": v(849, -108.26) * mm});
            skLineSegment(sketch, "E253.MirrorCS", {"start": v(850.72, -110.72) * mm, "end": v(847.44, -113.01) * mm});
            skLineSegment(sketch, "E254.bottom", {"start": v(464.5, 76.76) * mm, "end": v(462.78, 79.22) * mm});
            skLineSegment(sketch, "E254.top", {"start": v(467.77, 79.05) * mm, "end": v(466.05, 81.5) * mm});
            skLineSegment(sketch, "E254.left", {"start": v(464.5, 76.76) * mm, "end": v(467.77, 79.05) * mm});
            skLineSegment(sketch, "E254.right", {"start": v(462.78, 79.22) * mm, "end": v(466.05, 81.5) * mm});
            skLineSegment(sketch, "E255.bottom", {"start": v(657.33, -19.07) * mm, "end": v(653.9, -14.15) * mm});
            skLineSegment(sketch, "E255.top", {"start": v(659.8, -17.34) * mm, "end": v(656.35, -12.43) * mm});
            skLineSegment(sketch, "E255.left", {"start": v(657.33, -19.07) * mm, "end": v(659.8, -17.34) * mm});
            skLineSegment(sketch, "E255.right", {"start": v(653.9, -14.15) * mm, "end": v(656.35, -12.43) * mm});
            skLineSegment(sketch, "E256.bottom", {"start": v(1328.61, 202.88) * mm, "end": v(948.61, 202.88) * mm});
            skLineSegment(sketch, "E256.top", {"start": v(1328.61, -47.12) * mm, "end": v(948.61, -47.12) * mm});
            skLineSegment(sketch, "E256.left", {"start": v(1328.61, 202.88) * mm, "end": v(1328.61, -47.12) * mm});
            skLineSegment(sketch, "E256.right", {"start": v(948.61, 202.88) * mm, "end": v(948.61, -30.12) * mm});
            skLineSegment(sketch, "E257.left", {"start": v(948.61, -47.12) * mm, "end": v(948.61, -34.12) * mm});
            skLineSegment(sketch, "E257.right", {"start": v(952.61, -47.12) * mm, "end": v(952.61, -37.12) * mm});
            skLineSegment(sketch, "E258", {"start": v(952.61, -37.12) * mm, "end": v(956.61, -37.12) * mm});
            skLineSegment(sketch, "E259", {"start": v(952.61, 82.88) * mm, "end": v(956.61, 82.88) * mm});
            skLineSegment(sketch, "E260.MirrorCS", {"start": v(952.61, 72.88) * mm, "end": v(956.61, 72.88) * mm});
            skLineSegment(sketch, "E261", {"start": v(952.61, 187.88) * mm, "end": v(956.61, 187.88) * mm});
            skLineSegment(sketch, "E262", {"start": v(952.61, 177.88) * mm, "end": v(956.61, 177.88) * mm});
            skLineSegment(sketch, "E263.trimOffspring", {"start": v(956.61, 82.88) * mm, "end": v(956.61, 72.88) * mm});
            skLineSegment(sketch, "E264.trimOffspring", {"start": v(956.61, -37.12) * mm, "end": v(956.61, -47.12) * mm});
            skLineSegment(sketch, "E265", {"start": v(952.61, 187.88) * mm, "end": v(952.61, 177.88) * mm});
            skLineSegment(sketch, "E266", {"start": v(956.61, 187.88) * mm, "end": v(956.61, 177.88) * mm});
            skLineSegment(sketch, "E267", {"start": v(952.61, 82.88) * mm, "end": v(952.61, 72.88) * mm});
            skLineSegment(sketch, "E268", {"start": v(948.61, -34.12) * mm, "end": v(948.61, -30.12) * mm});
            skLineSegment(sketch, "E269", {"start": v(1138.61, 202.88) * mm, "end": v(1138.61, -47.12) * mm, "construction": true});
            skLineSegment(sketch, "E270.MirrorCS", {"start": v(1324.61, 187.88) * mm, "end": v(1320.61, 187.88) * mm});
            skLineSegment(sketch, "E271.MirrorCS", {"start": v(1328.61, -34.12) * mm, "end": v(1328.61, -30.12) * mm});
            skLineSegment(sketch, "E272.MirrorCS", {"start": v(1324.61, -37.12) * mm, "end": v(1320.61, -37.12) * mm});
            skLineSegment(sketch, "E273.MirrorCS", {"start": v(1324.61, 82.88) * mm, "end": v(1320.61, 82.88) * mm});
            skLineSegment(sketch, "E274.MirrorCS", {"start": v(1320.61, 82.88) * mm, "end": v(1320.61, 72.88) * mm});
            skLineSegment(sketch, "E275.MirrorCS", {"start": v(1324.61, 187.88) * mm, "end": v(1324.61, 177.88) * mm});
            skLineSegment(sketch, "E276.MirrorCS", {"start": v(1320.61, 187.88) * mm, "end": v(1320.61, 177.88) * mm});
            skLineSegment(sketch, "E277.MirrorCS", {"start": v(1324.61, 82.88) * mm, "end": v(1324.61, 72.88) * mm});
            skLineSegment(sketch, "E278.MirrorCS", {"start": v(1328.61, -47.12) * mm, "end": v(1328.61, -34.12) * mm});
            skLineSegment(sketch, "E279.MirrorCS", {"start": v(1324.61, -47.12) * mm, "end": v(1324.61, -37.12) * mm});
            skLineSegment(sketch, "E280.MirrorCS", {"start": v(1324.61, 72.88) * mm, "end": v(1320.61, 72.88) * mm});
            skLineSegment(sketch, "E281.MirrorCS", {"start": v(1324.61, 177.88) * mm, "end": v(1320.61, 177.88) * mm});
            skLineSegment(sketch, "E282.MirrorCS", {"start": v(1320.61, -37.12) * mm, "end": v(1320.61, -47.12) * mm});
            skSolve(sketch);
        }
        {
            var Q0;
            {var subQ0=sQuery(id+"F0.wireOp",EDGE,"E42.MirrorCS");Q0=makeQuery(id+"F0.imprint","IMPRINT",FACE,{"disambiguationData":[TD([[makeQuery(id+"F0.imprint","IMPRINT",EDGE,{"derivedFrom":subQ0}),1.0]])]});}
            var Q1;
            {var subQ0=sQuery(id+"F0.wireOp",EDGE,"E47");var subQ1=sQuery(id+"F0.wireOp",EDGE,"E45");var subQ2=makeQuery(id+"F0.imprint","INTERSECT",VERTEX,{"derivedFrom":[subQ1,subQ0]});Q1=makeQuery(id+"F0.imprint","IMPRINT",FACE,{"disambiguationData":[TD([[makeQuery(id+"F0.imprint","IMPRINT",EDGE,{"disambiguationData":[TD([[subQ2,-1.0]])],"derivedFrom":subQ1}),-1.0]])]});}
            var Q2;
            {var subQ8=sQuery(id+"F0.wireOp",EDGE,"E0.bottom");Q2=makeQuery(id+"F0.imprint","IMPRINT",FACE,{"disambiguationData":[TD([[makeQuery(id+"F0.imprint","IMPRINT",EDGE,{"derivedFrom":subQ8}),1.0]])]});}
            var Q3;
            {var subQ14=sQuery(id+"F0.wireOp",EDGE,"E2.top");Q3=makeQuery(id+"F0.imprint","IMPRINT",FACE,{"disambiguationData":[TD([[makeQuery(id+"F0.imprint","IMPRINT",EDGE,{"derivedFrom":subQ14}),-1.0]])]});}
            var Q4;
            {var subQ0=sQuery(id+"F0.wireOp",EDGE,"E11.MirrorCS");Q4=makeQuery(id+"F0.imprint","IMPRINT",FACE,{"disambiguationData":[TD([[makeQuery(id+"F0.imprint","IMPRINT",EDGE,{"derivedFrom":subQ0}),-1.0]])]});}
            var Q5;
            {var subQ0=sQuery(id+"F0.wireOp",EDGE,"E40.MirrorCS");Q5=makeQuery(id+"F0.imprint","IMPRINT",FACE,{"disambiguationData":[TD([[makeQuery(id+"F0.imprint","IMPRINT",EDGE,{"derivedFrom":subQ0}),1.0]])]});}
            var Q6;
            {var subQ0=sQuery(id+"F0.wireOp",EDGE,"E15");Q6=makeQuery(id+"F0.imprint","IMPRINT",FACE,{"disambiguationData":[TD([[makeQuery(id+"F0.imprint","IMPRINT",EDGE,{"derivedFrom":subQ0}),1.0]])]});}
            var Q7;
            {var subQ0=sQuery(id+"F0.wireOp",EDGE,"E34.MirrorCS");Q7=makeQuery(id+"F0.imprint","IMPRINT",FACE,{"disambiguationData":[TD([[makeQuery(id+"F0.imprint","IMPRINT",EDGE,{"derivedFrom":subQ0}),1.0]])]});}
            var Q8;
            {var subQ0=sQuery(id+"F0.wireOp",EDGE,"E69.MirrorCS");var subQ3=makeQuery(id+"F0.imprint","INTERSECT",VERTEX,{"derivedFrom":[sQuery(id+"F0.wireOp",EDGE,"E43.MirrorCS"),subQ0]});Q8=makeQuery(id+"F0.imprint","IMPRINT",FACE,{"disambiguationData":[TD([[makeQuery(id+"F0.imprint","IMPRINT",EDGE,{"disambiguationData":[TD([[subQ3,-1.0]])],"derivedFrom":subQ0}),-1.0]])]});}
            var Q9;
            {var subQ0=sQuery(id+"F0.wireOp",EDGE,"E16.MirrorCS");Q9=makeQuery(id+"F0.imprint","IMPRINT",FACE,{"disambiguationData":[TD([[makeQuery(id+"F0.imprint","IMPRINT",EDGE,{"derivedFrom":subQ0}),-1.0]])]});}
            var Q10;
            {var subQ0=sQuery(id+"F0.wireOp",EDGE,"E10.bottom");Q10=makeQuery(id+"F0.imprint","IMPRINT",FACE,{"disambiguationData":[TD([[makeQuery(id+"F0.imprint","IMPRINT",EDGE,{"derivedFrom":subQ0}),-1.0]])]});}
            var Q11;
            {var subQ0=sQuery(id+"F0.wireOp",EDGE,"E57.trimOffspring");var subQ1=makeQuery(id+"F0.imprint","INTERSECT",VERTEX,{"derivedFrom":[sQuery(id+"F0.wireOp",EDGE,"E15"),subQ0]});Q11=makeQuery(id+"F0.imprint","IMPRINT",FACE,{"disambiguationData":[TD([[makeQuery(id+"F0.imprint","IMPRINT",EDGE,{"disambiguationData":[TD([[subQ1,-1.0]])],"derivedFrom":subQ0}),1.0]])]});}
            var Q12;
            {var subQ0=sQuery(id+"F0.wireOp",EDGE,"E57.trimOffspring");var subQ3=sQuery(id+"F0.wireOp",EDGE,"E36.MirrorCS");var subQ4=makeQuery(id+"F0.imprint","INTERSECT",VERTEX,{"derivedFrom":[subQ3,subQ0]});Q12=makeQuery(id+"F0.imprint","IMPRINT",FACE,{"disambiguationData":[TD([[makeQuery(id+"F0.imprint","IMPRINT",EDGE,{"disambiguationData":[TD([[subQ4,-1.0]])],"derivedFrom":subQ3}),1.0]])]});}
            var Q13;
            {var subQ1=sQuery(id+"F0.wireOp",EDGE,"E45");var subQ3=sQuery(id+"F0.wireOp",EDGE,"E47");var subQ4=makeQuery(id+"F0.imprint","INTERSECT",VERTEX,{"derivedFrom":[subQ1,subQ3]});Q13=makeQuery(id+"F0.imprint","IMPRINT",FACE,{"disambiguationData":[TD([[makeQuery(id+"F0.imprint","IMPRINT",EDGE,{"disambiguationData":[TD([[subQ4,1.0]])],"derivedFrom":subQ3}),-1.0]])]});}
            var Q14;
            {var subQ0=sQuery(id+"F0.wireOp",EDGE,"E47");var subQ1=sQuery(id+"F0.wireOp",EDGE,"E45");var subQ2=makeQuery(id+"F0.imprint","INTERSECT",VERTEX,{"derivedFrom":[subQ1,subQ0]});Q14=makeQuery(id+"F0.imprint","IMPRINT",FACE,{"disambiguationData":[TD([[makeQuery(id+"F0.imprint","IMPRINT",EDGE,{"disambiguationData":[TD([[subQ2,-1.0]])],"derivedFrom":subQ1}),1.0]])]});}
            var Q15;
            {var subQ1=sQuery(id+"F0.wireOp",EDGE,"E61.MirrorCS");Q15=makeQuery(id+"F0.imprint","IMPRINT",FACE,{"disambiguationData":[TD([[makeQuery(id+"F0.imprint","IMPRINT",EDGE,{"derivedFrom":subQ1}),1.0]])]});}
            var Q16;
            {var subQ1=sQuery(id+"F0.wireOp",EDGE,"E3.top");Q16=makeQuery(id+"F0.imprint","IMPRINT",FACE,{"disambiguationData":[TD([[makeQuery(id+"F0.imprint","IMPRINT",EDGE,{"derivedFrom":subQ1}),1.0]])]});}
            var Q17;
            {var subQ1=sQuery(id+"F0.wireOp",EDGE,"E12");Q17=makeQuery(id+"F0.imprint","IMPRINT",FACE,{"disambiguationData":[TD([[makeQuery(id+"F0.imprint","IMPRINT",EDGE,{"derivedFrom":subQ1}),1.0]])]});}
            var Q18;
            Q18=makeQuery(id+"F0.imprint","IMPRINT",FACE,{"disambiguationData":[TD([[makeQuery(id+"F0.imprint","IMPRINT",EDGE,{"derivedFrom":sQuery(id+"F0.wireOp",EDGE,"E11.MirrorCS")}),1.0]])]});
            var Q19;
            {var subQ4=sQuery(id+"F0.wireOp",EDGE,"E49.trimOffspring");Q19=makeQuery(id+"F0.imprint","IMPRINT",FACE,{"disambiguationData":[TD([[makeQuery(id+"F0.imprint","IMPRINT",EDGE,{"derivedFrom":subQ4}),-1.0]])]});}
            var Q20;
            {var subQ0=sQuery(id+"F0.wireOp",EDGE,"E70");Q20=makeQuery(id+"F0.imprint","IMPRINT",FACE,{"disambiguationData":[TD([[makeQuery(id+"F0.imprint","IMPRINT",EDGE,{"derivedFrom":subQ0}),-1.0]])]});}
            var Q21;
            {var subQ0=sQuery(id+"F0.wireOp",EDGE,"E60.MirrorCS");Q21=makeQuery(id+"F0.imprint","IMPRINT",FACE,{"disambiguationData":[TD([[makeQuery(id+"F0.imprint","IMPRINT",EDGE,{"derivedFrom":subQ0}),1.0]])]});}
            var Q22;
            {var subQ0=sQuery(id+"F0.wireOp",EDGE,"E44.MirrorCS");Q22=makeQuery(id+"F0.imprint","IMPRINT",FACE,{"disambiguationData":[TD([[makeQuery(id+"F0.imprint","IMPRINT",EDGE,{"derivedFrom":subQ0}),-1.0]])]});}
            var Q23;
            {var subQ0=sQuery(id+"F0.wireOp",EDGE,"E3.bottom");Q23=makeQuery(id+"F0.imprint","IMPRINT",FACE,{"disambiguationData":[TD([[makeQuery(id+"F0.imprint","IMPRINT",EDGE,{"derivedFrom":subQ0}),-1.0]])]});}
            var Q24;
            {var subQ6=sQuery(id+"F0.wireOp",EDGE,"E18");Q24=makeQuery(id+"F0.imprint","IMPRINT",FACE,{"disambiguationData":[TD([[makeQuery(id+"F0.imprint","IMPRINT",EDGE,{"derivedFrom":subQ6}),-1.0]])]});}
            var Q25;
            {var subQ3=sQuery(id+"F0.wireOp",EDGE,"E51");Q25=makeQuery(id+"F0.imprint","IMPRINT",FACE,{"disambiguationData":[TD([[makeQuery(id+"F0.imprint","IMPRINT",EDGE,{"derivedFrom":subQ3}),-1.0]])]});}
            var Q26;
            {var subQ1=sQuery(id+"F0.wireOp",EDGE,"tfAmf85F-RHVb-4QbN-3uL9-GZ0NnuUHbLcj.left");Q26=makeQuery(id+"F0.imprint","IMPRINT",FACE,{"disambiguationData":[TD([[makeQuery(id+"F0.imprint","IMPRINT",EDGE,{"derivedFrom":subQ1}),-1.0]])]});}
            var Q27;
            {var subQ5=sQuery(id+"F0.wireOp",EDGE,"E144.right");Q27=makeQuery(id+"F0.imprint","IMPRINT",FACE,{"disambiguationData":[TD([[makeQuery(id+"F0.imprint","IMPRINT",EDGE,{"derivedFrom":subQ5}),-1.0]])]});}
            var Q28;
            {var subQ5=sQuery(id+"F0.wireOp",EDGE,"E148.MirrorCS");Q28=makeQuery(id+"F0.imprint","IMPRINT",FACE,{"disambiguationData":[TD([[makeQuery(id+"F0.imprint","IMPRINT",EDGE,{"derivedFrom":subQ5}),1.0]])]});}
            var Q29;
            {var subQ5=sQuery(id+"F0.wireOp",EDGE,"40aa9182-da7a-4239-aef8-64ec93e78b944.MirrorCS");Q29=makeQuery(id+"F0.imprint","IMPRINT",FACE,{"disambiguationData":[TD([[makeQuery(id+"F0.imprint","IMPRINT",EDGE,{"derivedFrom":subQ5}),1.0]])]});}
            var Q30;
            Q30=makeQuery(id+"F0.imprint","IMPRINT",FACE,{"disambiguationData":[TD([[makeQuery(id+"F0.imprint","IMPRINT",EDGE,{"derivedFrom":sQuery(id+"F0.wireOp",EDGE,"E163.bottom")}),-1.0]])]});
            extrude(context, id + "F1", {"entities" : qUnion([Q0, Q1, Q2, Q3, Q4, Q5, Q6, Q7, Q8, Q9, Q10, Q11, Q12, Q13, Q14, Q15, Q16, Q17, Q18, Q19, Q20, Q21, Q22, Q23, Q24, Q25, Q26, Q27, Q28, Q29, Q30]), "depth" : 4 * mm});
        }
        {
            var Q0;
            {var subQ5=sQuery(id+"F0.wireOp",EDGE,"E18");Q0=makeQuery(id+"F0.imprint","IMPRINT",FACE,{"disambiguationData":[TD([[makeQuery(id+"F0.imprint","IMPRINT",EDGE,{"derivedFrom":subQ5}),-1.0]])]});}
            var Q1;
            {var subQ0=sQuery(id+"F0.wireOp",EDGE,"E54");Q1=makeQuery(id+"F0.imprint","IMPRINT",FACE,{"disambiguationData":[TD([[makeQuery(id+"F0.imprint","IMPRINT",EDGE,{"derivedFrom":subQ0}),1.0]])]});}
            var Q2;
            {var subQ0=sQuery(id+"F0.wireOp",EDGE,"E47");var subQ1=sQuery(id+"F0.wireOp",EDGE,"E45");var subQ2=makeQuery(id+"F0.imprint","INTERSECT",VERTEX,{"derivedFrom":[subQ1,subQ0]});Q2=makeQuery(id+"F0.imprint","IMPRINT",FACE,{"disambiguationData":[TD([[makeQuery(id+"F0.imprint","IMPRINT",EDGE,{"disambiguationData":[TD([[subQ2,-1.0]])],"derivedFrom":subQ1}),1.0]])]});}
            var Q3;
            {var subQ0=sQuery(id+"F0.wireOp",EDGE,"E47");var subQ1=sQuery(id+"F0.wireOp",EDGE,"E45");var subQ2=makeQuery(id+"F0.imprint","INTERSECT",VERTEX,{"derivedFrom":[subQ1,subQ0]});Q3=makeQuery(id+"F0.imprint","IMPRINT",FACE,{"disambiguationData":[TD([[makeQuery(id+"F0.imprint","IMPRINT",EDGE,{"disambiguationData":[TD([[subQ2,-1.0]])],"derivedFrom":subQ1}),-1.0]])]});}
            var Q4;
            {var subQ0=sQuery(id+"F0.wireOp",EDGE,"E44.MirrorCS");Q4=makeQuery(id+"F0.imprint","IMPRINT",FACE,{"disambiguationData":[TD([[makeQuery(id+"F0.imprint","IMPRINT",EDGE,{"derivedFrom":subQ0}),-1.0]])]});}
            var Q5;
            {var subQ0=sQuery(id+"F0.wireOp",EDGE,"E62.MirrorCS");Q5=makeQuery(id+"F0.imprint","IMPRINT",FACE,{"disambiguationData":[TD([[makeQuery(id+"F0.imprint","IMPRINT",EDGE,{"derivedFrom":subQ0}),-1.0]])]});}
            var Q6;
            {var subQ0=sQuery(id+"F0.wireOp",EDGE,"E60.MirrorCS");Q6=makeQuery(id+"F0.imprint","IMPRINT",FACE,{"disambiguationData":[TD([[makeQuery(id+"F0.imprint","IMPRINT",EDGE,{"derivedFrom":subQ0}),1.0]])]});}
            extrude(context, id + "F2", {"entities" : qUnion([Q0, Q1, Q2, Q3, Q4, Q5, Q6]), "depth" : 4 * mm});
        }
        {
            var Q0;
            {var subQ1=sQuery(id+"F0.wireOp",EDGE,"E45");var subQ3=sQuery(id+"F0.wireOp",EDGE,"E47");var subQ4=makeQuery(id+"F0.imprint","INTERSECT",VERTEX,{"derivedFrom":[subQ1,subQ3]});Q0=makeQuery(id+"F0.imprint","IMPRINT",FACE,{"disambiguationData":[TD([[makeQuery(id+"F0.imprint","IMPRINT",EDGE,{"disambiguationData":[TD([[subQ4,1.0]])],"derivedFrom":subQ3}),-1.0]])]});}
            var Q1;
            {var subQ1=sQuery(id+"F0.wireOp",EDGE,"E12");Q1=makeQuery(id+"F0.imprint","IMPRINT",FACE,{"disambiguationData":[TD([[makeQuery(id+"F0.imprint","IMPRINT",EDGE,{"derivedFrom":subQ1}),1.0]])]});}
            var Q2;
            {var subQ0=sQuery(id+"F0.wireOp",EDGE,"E53");Q2=makeQuery(id+"F0.imprint","IMPRINT",FACE,{"disambiguationData":[TD([[makeQuery(id+"F0.imprint","IMPRINT",EDGE,{"derivedFrom":subQ0}),1.0]])]});}
            var Q3;
            {var subQ0=sQuery(id+"F0.wireOp",EDGE,"E47");var subQ1=sQuery(id+"F0.wireOp",EDGE,"E45");var subQ2=makeQuery(id+"F0.imprint","INTERSECT",VERTEX,{"derivedFrom":[subQ1,subQ0]});Q3=makeQuery(id+"F0.imprint","IMPRINT",FACE,{"disambiguationData":[TD([[makeQuery(id+"F0.imprint","IMPRINT",EDGE,{"disambiguationData":[TD([[subQ2,-1.0]])],"derivedFrom":subQ1}),1.0]])]});}
            var Q4;
            {var subQ0=sQuery(id+"F0.wireOp",EDGE,"E11.MirrorCS");Q4=makeQuery(id+"F0.imprint","IMPRINT",FACE,{"disambiguationData":[TD([[makeQuery(id+"F0.imprint","IMPRINT",EDGE,{"derivedFrom":subQ0}),-1.0]])]});}
            var Q5;
            Q5=makeQuery(id+"F0.imprint","IMPRINT",FACE,{"disambiguationData":[TD([[makeQuery(id+"F0.imprint","IMPRINT",EDGE,{"derivedFrom":sQuery(id+"F0.wireOp",EDGE,"E11.MirrorCS")}),1.0]])]});
            var Q6;
            {var subQ0=sQuery(id+"F0.wireOp",EDGE,"E70");Q6=makeQuery(id+"F0.imprint","IMPRINT",FACE,{"disambiguationData":[TD([[makeQuery(id+"F0.imprint","IMPRINT",EDGE,{"derivedFrom":subQ0}),-1.0]])]});}
            var Q7;
            {var subQ0=sQuery(id+"F0.wireOp",EDGE,"E66.MirrorCS");Q7=makeQuery(id+"F0.imprint","IMPRINT",FACE,{"disambiguationData":[TD([[makeQuery(id+"F0.imprint","IMPRINT",EDGE,{"derivedFrom":subQ0}),-1.0]])]});}
            extrude(context, id + "F3", {"entities" : qUnion([Q0, Q1, Q2, Q3, Q4, Q5, Q6, Q7]), "depth" : 4 * mm});
        }
        {
            var Q0;
            Q0=makeQuery(id+"F0.imprint","IMPRINT",FACE,{"disambiguationData":[TD([[makeQuery(id+"F0.imprint","IMPRINT",EDGE,{"derivedFrom":sQuery(id+"F0.wireOp",EDGE,"E80")}),1.0]])]});
            var Q1;
            Q1=makeQuery(id+"F0.imprint","IMPRINT",FACE,{"disambiguationData":[TD([[makeQuery(id+"F0.imprint","IMPRINT",EDGE,{"derivedFrom":sQuery(id+"F0.wireOp",EDGE,"E4")}),1.0]])]});
            var Q2;
            Q2=makeQuery(id+"F0.imprint","IMPRINT",FACE,{"disambiguationData":[TD([[makeQuery(id+"F0.imprint","IMPRINT",EDGE,{"derivedFrom":sQuery(id+"F0.wireOp",EDGE,"E95")}),-1.0]])]});
            var Q3;
            {var subQ1=sQuery(id+"F0.wireOp",EDGE,"E173");Q3=makeQuery(id+"F0.imprint","IMPRINT",FACE,{"disambiguationData":[TD([[makeQuery(id+"F0.imprint","IMPRINT",EDGE,{"derivedFrom":subQ1}),1.0]])]});}
            var Q4;
            {var subQ0=sQuery(id+"F0.wireOp",EDGE,"E176");Q4=makeQuery(id+"F0.imprint","IMPRINT",FACE,{"disambiguationData":[TD([[makeQuery(id+"F0.imprint","IMPRINT",EDGE,{"derivedFrom":subQ0}),-1.0]])]});}
            var Q5;
            {var subQ0=sQuery(id+"F0.wireOp",EDGE,"E193");Q5=makeQuery(id+"F0.imprint","IMPRINT",FACE,{"disambiguationData":[TD([[makeQuery(id+"F0.imprint","IMPRINT",EDGE,{"derivedFrom":subQ0}),1.0]])]});}
            var Q6;
            {var subQ0=sQuery(id+"F0.wireOp",EDGE,"E193");Q6=makeQuery(id+"F0.imprint","IMPRINT",FACE,{"disambiguationData":[TD([[makeQuery(id+"F0.imprint","IMPRINT",EDGE,{"derivedFrom":subQ0}),-1.0]])]});}
            extrude(context, id + "F4", {"entities" : qUnion([Q0, Q1, Q2, Q3, Q4, Q5, Q6]), "depth" : 4 * mm});
        }
        {
            var Q0;
            Q0=makeQuery(id+"F0.imprint","IMPRINT",FACE,{"disambiguationData":[TD([[makeQuery(id+"F0.imprint","IMPRINT",EDGE,{"derivedFrom":sQuery(id+"F0.wireOp",EDGE,"E126")}),-1.0]])]});
            var Q1;
            {var subQ0=sQuery(id+"F0.wireOp",EDGE,"E100");Q1=makeQuery(id+"F0.imprint","IMPRINT",FACE,{"disambiguationData":[TD([[makeQuery(id+"F0.imprint","IMPRINT",EDGE,{"derivedFrom":subQ0}),1.0]])]});}
            var Q2;
            Q2=makeQuery(id+"F0.imprint","IMPRINT",FACE,{"disambiguationData":[TD([[makeQuery(id+"F0.imprint","IMPRINT",EDGE,{"derivedFrom":sQuery(id+"F0.wireOp",EDGE,"E132")}),1.0]])]});
            extrude(context, id + "F5", {"entities" : qUnion([Q0, Q1, Q2]), "depth" : 4 * mm});
        }
        {
            var Q0;
            Q0=makeQuery(id+"F2.opExtrude","SWEPT_FACE",FACE,{"disambiguationData":[OSD([sQuery(id+"F0.wireOp",EDGE,"E161.right")])]});
            var sketch = newSketch(context, id + "F6", { "sketchPlane" : qUnion([Q0])});
            skLineSegment(sketch, "E283.bottom", {"start": v(-94.84, 0) * mm, "end": v(-92.84, 0) * mm});
            skLineSegment(sketch, "E283.top", {"start": v(-96.84, 10) * mm, "end": v(-92.84, 10) * mm});
            skLineSegment(sketch, "E284.bottom", {"start": v(-88.84, 4) * mm, "end": v(108, 4) * mm});
            skLineSegment(sketch, "E284.top", {"start": v(-92.84, 10) * mm, "end": v(112, 10) * mm});
            skLineSegment(sketch, "E284.right", {"start": v(112, 4) * mm, "end": v(112, 10) * mm});
            skLineSegment(sketch, "E285.0.1", {"start": v(112, 0) * mm, "end": v(112, 4) * mm});
            skLineSegment(sketch, "E285.0.3", {"start": v(108, 4) * mm, "end": v(108, 0) * mm});
            skPoint(sketch, "E285.0.2.end.orphan", {"position": v(108, 4) * mm});
            skLineSegment(sketch, "E286.top", {"start": v(-96.84, -10) * mm, "end": v(-92.84, -10) * mm});
            skLineSegment(sketch, "E286.left", {"start": v(-96.84, 0) * mm, "end": v(-96.84, -10) * mm});
            skLineSegment(sketch, "E286.right", {"start": v(-92.84, 0) * mm, "end": v(-92.84, -10) * mm});
            skPoint(sketch, "E287.oppositeSnap0", {"position": v(-94.84, 0) * mm});
            skFitSpline(sketch, "E288", {"points": [v(-96.84, 10) * mm, v(-100.84, 4) * mm], "startDerivative": vector(-4.3, 0.57) * mm, "endDerivative": vector(1.18, -14.2) * mm});
            skLineSegment(sketch, "E289", {"start": v(112, 4) * mm, "end": v(117.7, 4) * mm});
            skLineSegment(sketch, "E290", {"start": v(108, 0) * mm, "end": v(108, -10) * mm});
            skLineSegment(sketch, "E291", {"start": v(108, -10) * mm, "end": v(112, -10) * mm});
            skLineSegment(sketch, "E292", {"start": v(112, -10) * mm, "end": v(112, 0) * mm});
            skFitSpline(sketch, "E293", {"points": [v(112, 10) * mm, v(117.7, 4) * mm], "startDerivative": vector(11.43, 0.2) * mm, "endDerivative": vector(0.16, -10.43) * mm});
            skPoint(sketch, "E287.right.end.orphan", {"position": v(-100.84, 0) * mm});
            skLineSegment(sketch, "E294", {"start": v(-100.84, 4) * mm, "end": v(-100.84, 2) * mm});
            skLineSegment(sketch, "E295", {"start": v(-100.84, 2) * mm, "end": v(-96.84, 2) * mm});
            skLineSegment(sketch, "E296", {"start": v(-88.84, 2) * mm, "end": v(-88.84, 4) * mm});
            skLineSegment(sketch, "E297", {"start": v(-92.84, 0) * mm, "end": v(-92.84, 2) * mm});
            skLineSegment(sketch, "E298", {"start": v(-96.84, 0) * mm, "end": v(-96.84, 2) * mm});
            skLineSegment(sketch, "E299.trimOffspring", {"start": v(-92.84, 2) * mm, "end": v(-88.84, 2) * mm});
            skLineSegment(sketch, "E300", {"start": v(-100.84, 2) * mm, "end": v(-100.84, 0) * mm});
            skLineSegment(sketch, "E301", {"start": v(-88.84, 2) * mm, "end": v(-88.84, 0) * mm});
            skLineSegment(sketch, "E302", {"start": v(-88.84, 0) * mm, "end": v(-100.84, 0) * mm});
            skLineSegment(sketch, "E303", {"start": v(-100.84, 0) * mm, "end": v(-100.84, -2) * mm});
            skLineSegment(sketch, "E304", {"start": v(-100.84, -2) * mm, "end": v(-88.84, -2) * mm});
            skLineSegment(sketch, "E305", {"start": v(-88.84, -2) * mm, "end": v(-88.84, 0) * mm});
            skLineSegment(sketch, "E306.top", {"start": v(-60.3, -170.8) * mm, "end": v(-56.3, -170.8) * mm});
            skLineSegment(sketch, "E307.bottom", {"start": v(-52.3, -176.8) * mm, "end": v(144.55, -176.8) * mm});
            skLineSegment(sketch, "E307.top", {"start": v(-56.3, -170.8) * mm, "end": v(148.55, -170.8) * mm});
            skLineSegment(sketch, "E308.0.1", {"start": v(148.55, -180.8) * mm, "end": v(148.55, -176.8) * mm});
            skLineSegment(sketch, "E308.0.3", {"start": v(144.55, -176.8) * mm, "end": v(144.55, -180.8) * mm});
            skPoint(sketch, "E308.0.2.end.orphan", {"position": v(144.55, -176.8) * mm});
            skLineSegment(sketch, "E309.top", {"start": v(-60.3, -190.8) * mm, "end": v(-56.3, -190.8) * mm});
            skLineSegment(sketch, "E309.left", {"start": v(-60.3, -182.8) * mm, "end": v(-60.3, -190.8) * mm});
            skLineSegment(sketch, "E309.right", {"start": v(-56.3, -182.8) * mm, "end": v(-56.3, -190.8) * mm});
            skPoint(sketch, "E310.oppositeSnap0", {"position": v(-58.3, -180.8) * mm});
            skFitSpline(sketch, "E311", {"points": [v(-60.3, -170.8) * mm, v(-64.3, -176.8) * mm], "startDerivative": vector(-4.3, 0.57) * mm, "endDerivative": vector(1.18, -14.2) * mm});
            skLineSegment(sketch, "E312", {"start": v(148.55, -176.8) * mm, "end": v(154.24, -176.8) * mm});
            skLineSegment(sketch, "E313", {"start": v(144.55, -180.8) * mm, "end": v(144.55, -190.8) * mm});
            skLineSegment(sketch, "E314", {"start": v(144.55, -190.8) * mm, "end": v(148.55, -190.8) * mm});
            skLineSegment(sketch, "E315", {"start": v(148.55, -190.8) * mm, "end": v(148.55, -180.8) * mm});
            skFitSpline(sketch, "E316", {"points": [v(148.55, -170.8) * mm, v(154.24, -176.8) * mm], "startDerivative": vector(11.43, 0.2) * mm, "endDerivative": vector(0.16, -10.43) * mm});
            skPoint(sketch, "E310.right.end.orphan", {"position": v(-64.3, -180.8) * mm});
            skLineSegment(sketch, "E317", {"start": v(-64.3, -176.8) * mm, "end": v(-64.3, -178.8) * mm});
            skLineSegment(sketch, "E318", {"start": v(-52.3, -178.8) * mm, "end": v(-52.3, -176.8) * mm});
            skLineSegment(sketch, "E319", {"start": v(-64.3, -178.8) * mm, "end": v(-64.3, -180.8) * mm});
            skLineSegment(sketch, "E320", {"start": v(-52.3, -178.8) * mm, "end": v(-52.3, -180.8) * mm});
            skLineSegment(sketch, "E321", {"start": v(-64.3, -180.8) * mm, "end": v(-64.3, -182.8) * mm});
            skLineSegment(sketch, "E322", {"start": v(-64.3, -182.8) * mm, "end": v(-60.3, -182.8) * mm});
            skLineSegment(sketch, "E323", {"start": v(-52.3, -182.8) * mm, "end": v(-52.3, -180.8) * mm});
            skPoint(sketch, "E306.bottom.end.orphan", {"position": v(-56.3, -180.8) * mm});
            skPoint(sketch, "E324.end.orphan", {"position": v(-60.3, -180.8) * mm});
            skLineSegment(sketch, "E325.trimOffspring", {"start": v(-56.3, -182.8) * mm, "end": v(-52.3, -182.8) * mm});
            skSolve(sketch);
        }
        {
            var Q0;
            Q0=qSketchRegion(id+"F6",true);
            extrude(context, id + "F7", {"entities" : qUnion([Q0]), "depth" : 3 * mm});
        }
        {
            var Q0;
            {var subQ4=sQuery(id+"F0.wireOp",EDGE,"E164.top");Q0=makeQuery(id+"F0.imprint","IMPRINT",FACE,{"disambiguationData":[TD([[makeQuery(id+"F0.imprint","IMPRINT",EDGE,{"derivedFrom":subQ4}),-1.0]])]});}
            var Q1;
            {var subQ5=sQuery(id+"F0.wireOp",EDGE,"E165.top");Q1=makeQuery(id+"F0.imprint","IMPRINT",FACE,{"disambiguationData":[TD([[makeQuery(id+"F0.imprint","IMPRINT",EDGE,{"derivedFrom":subQ5}),1.0]])]});}
            var Q2;
            {var subQ5=sQuery(id+"F0.wireOp",EDGE,"E165.bottom");Q2=makeQuery(id+"F0.imprint","IMPRINT",FACE,{"disambiguationData":[TD([[makeQuery(id+"F0.imprint","IMPRINT",EDGE,{"derivedFrom":subQ5}),-1.0]])]});}
            var Q3;
            Q3=makeQuery(id+"F0.imprint","IMPRINT",FACE,{"disambiguationData":[TD([[makeQuery(id+"F0.imprint","IMPRINT",EDGE,{"derivedFrom":sQuery(id+"F0.wireOp",EDGE,"E165.bottom")}),1.0]])]});
            extrude(context, id + "F8", {"entities" : qUnion([Q0, Q1, Q2, Q3]), "depth" : 3 * mm});
        }
        {
            var Q0;
            {var subQ1=sQuery(id+"F0.wireOp",EDGE,"E173");Q0=makeQuery(id+"F0.imprint","IMPRINT",FACE,{"disambiguationData":[TD([[makeQuery(id+"F0.imprint","IMPRINT",EDGE,{"derivedFrom":subQ1}),1.0]])]});}
            var Q1;
            {var subQ0=sQuery(id+"F0.wireOp",EDGE,"E180");Q1=makeQuery(id+"F0.imprint","IMPRINT",FACE,{"disambiguationData":[TD([[makeQuery(id+"F0.imprint","IMPRINT",EDGE,{"derivedFrom":subQ0}),1.0]])]});}
            var Q2;
            {var subQ0=sQuery(id+"F0.wireOp",EDGE,"E176");Q2=makeQuery(id+"F0.imprint","IMPRINT",FACE,{"disambiguationData":[TD([[makeQuery(id+"F0.imprint","IMPRINT",EDGE,{"derivedFrom":subQ0}),-1.0]])]});}
            var Q3;
            {var subQ1=sQuery(id+"F0.wireOp",EDGE,"E194");Q3=makeQuery(id+"F0.imprint","IMPRINT",FACE,{"disambiguationData":[TD([[makeQuery(id+"F0.imprint","IMPRINT",EDGE,{"derivedFrom":subQ1}),1.0]])]});}
            var Q4;
            {var subQ0=sQuery(id+"F0.wireOp",EDGE,"E193");Q4=makeQuery(id+"F0.imprint","IMPRINT",FACE,{"disambiguationData":[TD([[makeQuery(id+"F0.imprint","IMPRINT",EDGE,{"derivedFrom":subQ0}),1.0]])]});}
            var Q5;
            {var subQ0=sQuery(id+"F0.wireOp",EDGE,"E193");Q5=makeQuery(id+"F0.imprint","IMPRINT",FACE,{"disambiguationData":[TD([[makeQuery(id+"F0.imprint","IMPRINT",EDGE,{"derivedFrom":subQ0}),-1.0]])]});}
            extrude(context, id + "F9", {"entities" : qUnion([Q0, Q1, Q2, Q3, Q4, Q5]), "depth" : 8 * mm});
        }
        {
            var Q0;
            {var subQ4=sQuery(id+"F0.wireOp",EDGE,"E182.bottom");Q0=makeQuery(id+"F0.imprint","IMPRINT",FACE,{"disambiguationData":[TD([[makeQuery(id+"F0.imprint","IMPRINT",EDGE,{"derivedFrom":subQ4}),-1.0]])]});}
            var Q1;
            {var subQ0=sQuery(id+"F0.wireOp",EDGE,"E190.MirrorCS");Q1=makeQuery(id+"F0.imprint","IMPRINT",FACE,{"disambiguationData":[TD([[makeQuery(id+"F0.imprint","IMPRINT",EDGE,{"derivedFrom":subQ0}),-1.0]])]});}
            var Q2;
            {var subQ0=sQuery(id+"F0.wireOp",EDGE,"E186");Q2=makeQuery(id+"F0.imprint","IMPRINT",FACE,{"disambiguationData":[TD([[makeQuery(id+"F0.imprint","IMPRINT",EDGE,{"derivedFrom":subQ0}),1.0]])]});}
            var Q3;
            {var subQ1=sQuery(id+"F0.wireOp",EDGE,"E183");var subQ3=makeQuery(id+"F0.imprint","IMPRINT",VERTEX,{"derivedFrom":subQ1});Q3=makeQuery(id+"F0.imprint","IMPRINT",FACE,{"disambiguationData":[TD([[makeQuery(id+"F0.imprint","IMPRINT",EDGE,{"disambiguationData":[TD([[subQ3,-1.0]])],"derivedFrom":subQ1}),-1.0]])]});}
            var Q4;
            Q4=makeQuery(id+"F0.imprint","IMPRINT",FACE,{"disambiguationData":[TD([[makeQuery(id+"F0.imprint","IMPRINT",EDGE,{"derivedFrom":sQuery(id+"F0.wireOp",EDGE,"E182.top")}),-1.0]])]});
            var Q5;
            Q5=makeQuery(id+"F0.imprint","IMPRINT",FACE,{"disambiguationData":[TD([[makeQuery(id+"F0.imprint","IMPRINT",EDGE,{"derivedFrom":sQuery(id+"F0.wireOp",EDGE,"E181.bottom")}),-1.0]])]});
            var Q6;
            {var subQ0=sQuery(id+"F0.wireOp",EDGE,"E184");Q6=makeQuery(id+"F0.imprint","IMPRINT",FACE,{"disambiguationData":[TD([[makeQuery(id+"F0.imprint","IMPRINT",EDGE,{"derivedFrom":subQ0}),1.0]])]});}
            extrude(context, id + "F10", {"entities" : qUnion([Q0, Q1, Q2, Q3, Q4, Q5, Q6]), "depth" : 8 * mm});
        }
    });
